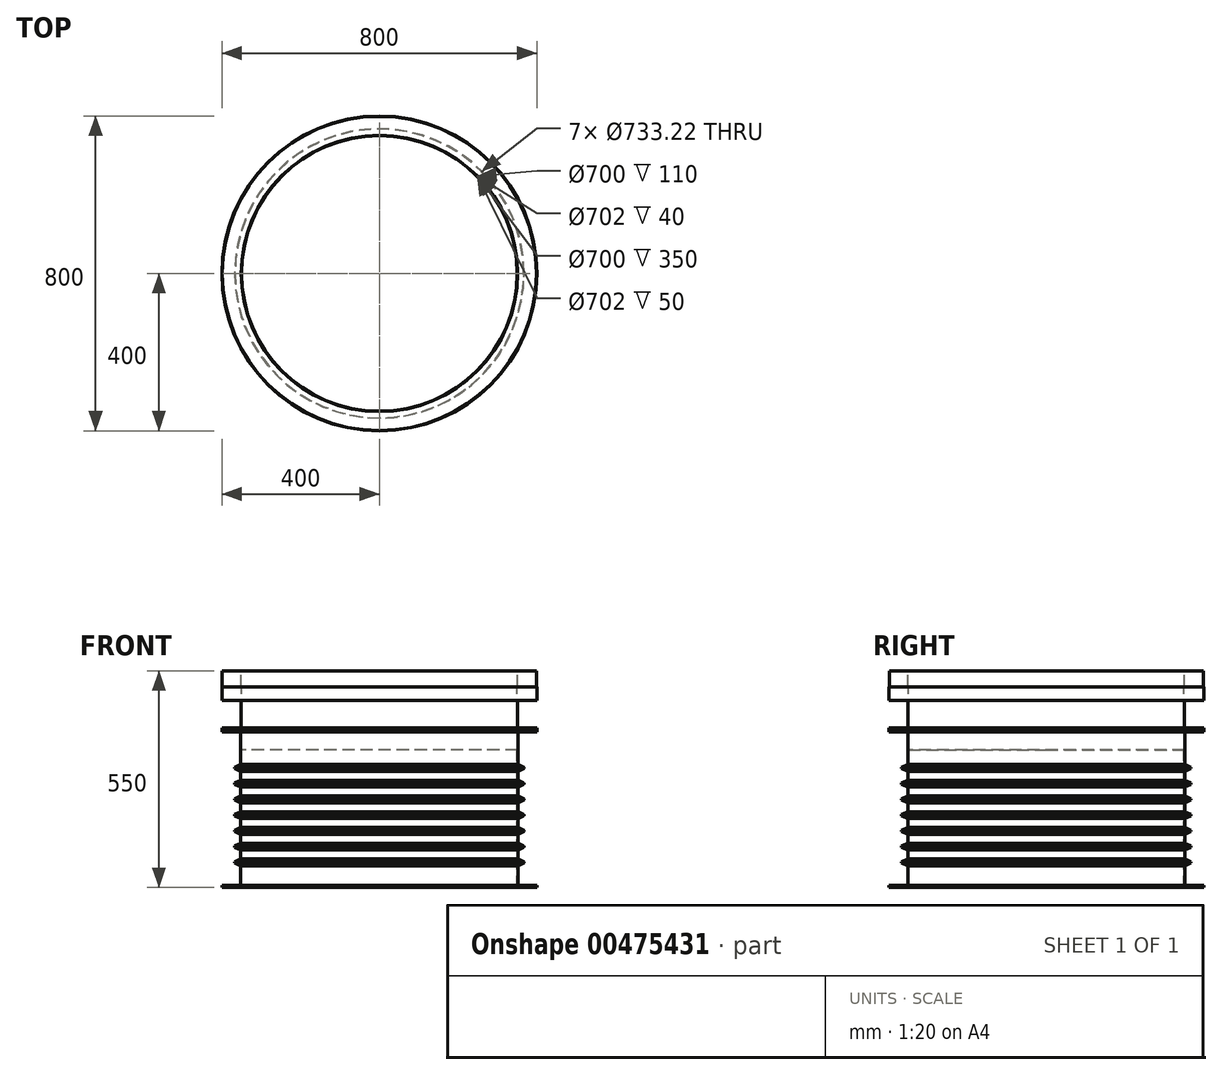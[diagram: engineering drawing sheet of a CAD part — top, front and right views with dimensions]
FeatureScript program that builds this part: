
annotation { "Feature Type Name" : "Feature", "Feature Type Description" : "" }
export const myFeature = defineFeature(function(context is Context, id is Id, definition is map)
    precondition{}
    {
        {
            var Q0;
            Q0=qCreatedBy(makeId("Front.planeOp"),FACE);
            var sketch = newSketch(context, id + "F0", { "sketchPlane" : qUnion([Q0])});
            skLineSegment(sketch, "E0", {"start": v(0, 1099) * mm, "end": v(0, -704.58) * mm, "construction": true});
            skLineSegment(sketch, "E1", {"start": v(-350, 330.96) * mm, "end": v(-350, 680.96) * mm});
            skLineSegment(sketch, "E2", {"start": v(-351, 680.96) * mm, "end": v(-351, 335.96) * mm});
            skLineSegment(sketch, "E3", {"start": v(-351, 335.96) * mm, "end": v(-400, 335.96) * mm});
            skLineSegment(sketch, "E4", {"start": v(-400, 335.96) * mm, "end": v(-400, 330.96) * mm});
            skLineSegment(sketch, "E5", {"start": v(-400, 330.96) * mm, "end": v(-350, 330.96) * mm});
            skLineSegment(sketch, "E6", {"start": v(-350, 680.96) * mm, "end": v(-351, 680.96) * mm});
            skLineSegment(sketch, "E7", {"start": v(-352, 335.96) * mm, "end": v(-352, 385.96) * mm});
            skLineSegment(sketch, "E8", {"start": v(-352, 385.96) * mm, "end": v(-367.6, 393.24) * mm});
            skLineSegment(sketch, "E9", {"start": v(-367.6, 393.24) * mm, "end": v(-367.6, 396.24) * mm});
            skLineSegment(sketch, "E10", {"start": v(-367.6, 396.24) * mm, "end": v(-352, 403.52) * mm});
            skLineSegment(sketch, "E11", {"start": v(-352, 425.96) * mm, "end": v(-352, 403.52) * mm});
            skLineSegment(sketch, "E12", {"start": v(-351, 402.88) * mm, "end": v(-366.6, 395.6) * mm});
            skLineSegment(sketch, "E13", {"start": v(-366.6, 395.6) * mm, "end": v(-366.6, 393.87) * mm});
            skLineSegment(sketch, "E14", {"start": v(-366.6, 393.87) * mm, "end": v(-351, 386.6) * mm});
            skLineSegment(sketch, "E15.0.1.0", {"start": v(-351, 442.88) * mm, "end": v(-366.6, 435.6) * mm});
            skLineSegment(sketch, "E15.0.1.1", {"start": v(-367.6, 436.24) * mm, "end": v(-352, 443.52) * mm});
            skLineSegment(sketch, "E15.0.1.2", {"start": v(-352, 425.96) * mm, "end": v(-367.6, 433.24) * mm});
            skLineSegment(sketch, "E15.0.1.3", {"start": v(-367.6, 433.24) * mm, "end": v(-367.6, 436.24) * mm});
            skLineSegment(sketch, "E15.0.1.4", {"start": v(-352, 465.96) * mm, "end": v(-352, 443.52) * mm});
            skLineSegment(sketch, "E15.0.1.5", {"start": v(-366.6, 433.87) * mm, "end": v(-351, 426.6) * mm});
            skLineSegment(sketch, "E15.0.1.6", {"start": v(-366.6, 435.6) * mm, "end": v(-366.6, 433.87) * mm});
            skLineSegment(sketch, "E15.0.2.0", {"start": v(-351, 482.88) * mm, "end": v(-366.6, 475.6) * mm});
            skLineSegment(sketch, "E15.0.2.1", {"start": v(-367.6, 476.24) * mm, "end": v(-352, 483.52) * mm});
            skLineSegment(sketch, "E15.0.2.2", {"start": v(-352, 465.96) * mm, "end": v(-367.6, 473.24) * mm});
            skLineSegment(sketch, "E15.0.2.3", {"start": v(-367.6, 473.24) * mm, "end": v(-367.6, 476.24) * mm});
            skLineSegment(sketch, "E15.0.2.4", {"start": v(-352, 505.96) * mm, "end": v(-352, 483.52) * mm});
            skLineSegment(sketch, "E15.0.2.5", {"start": v(-366.6, 473.87) * mm, "end": v(-351, 466.6) * mm});
            skLineSegment(sketch, "E15.0.2.6", {"start": v(-366.6, 475.6) * mm, "end": v(-366.6, 473.87) * mm});
            skLineSegment(sketch, "E15.0.3.0", {"start": v(-351, 522.88) * mm, "end": v(-366.6, 515.6) * mm});
            skLineSegment(sketch, "E15.0.3.1", {"start": v(-367.6, 516.24) * mm, "end": v(-352, 523.52) * mm});
            skLineSegment(sketch, "E15.0.3.2", {"start": v(-352, 505.96) * mm, "end": v(-367.6, 513.24) * mm});
            skLineSegment(sketch, "E15.0.3.3", {"start": v(-367.6, 513.24) * mm, "end": v(-367.6, 516.24) * mm});
            skLineSegment(sketch, "E15.0.3.4", {"start": v(-352, 545.96) * mm, "end": v(-352, 523.52) * mm});
            skLineSegment(sketch, "E15.0.3.5", {"start": v(-366.6, 513.87) * mm, "end": v(-351, 506.6) * mm});
            skLineSegment(sketch, "E15.0.3.6", {"start": v(-366.6, 515.6) * mm, "end": v(-366.6, 513.87) * mm});
            skLineSegment(sketch, "E15.0.4.0", {"start": v(-351, 562.88) * mm, "end": v(-366.6, 555.6) * mm});
            skLineSegment(sketch, "E15.0.4.1", {"start": v(-367.6, 556.24) * mm, "end": v(-352, 563.52) * mm});
            skLineSegment(sketch, "E15.0.4.2", {"start": v(-352, 545.96) * mm, "end": v(-367.6, 553.24) * mm});
            skLineSegment(sketch, "E15.0.4.3", {"start": v(-367.6, 553.24) * mm, "end": v(-367.6, 556.24) * mm});
            skLineSegment(sketch, "E15.0.4.4", {"start": v(-352, 585.96) * mm, "end": v(-352, 563.52) * mm});
            skLineSegment(sketch, "E15.0.4.5", {"start": v(-366.6, 553.87) * mm, "end": v(-351, 546.6) * mm});
            skLineSegment(sketch, "E15.0.4.6", {"start": v(-366.6, 555.6) * mm, "end": v(-366.6, 553.87) * mm});
            skLineSegment(sketch, "E15.0.5.0", {"start": v(-351, 602.88) * mm, "end": v(-366.6, 595.6) * mm});
            skLineSegment(sketch, "E15.0.5.1", {"start": v(-367.6, 596.24) * mm, "end": v(-352, 603.52) * mm});
            skLineSegment(sketch, "E15.0.5.2", {"start": v(-352, 585.96) * mm, "end": v(-367.6, 593.24) * mm});
            skLineSegment(sketch, "E15.0.5.3", {"start": v(-367.6, 593.24) * mm, "end": v(-367.6, 596.24) * mm});
            skLineSegment(sketch, "E15.0.5.4", {"start": v(-352, 625.96) * mm, "end": v(-352, 603.52) * mm});
            skLineSegment(sketch, "E15.0.5.5", {"start": v(-366.6, 593.87) * mm, "end": v(-351, 586.6) * mm});
            skLineSegment(sketch, "E15.0.5.6", {"start": v(-366.6, 595.6) * mm, "end": v(-366.6, 593.87) * mm});
            skLineSegment(sketch, "E15.0.6.0", {"start": v(-351, 642.88) * mm, "end": v(-366.6, 635.6) * mm});
            skLineSegment(sketch, "E15.0.6.1", {"start": v(-367.6, 636.24) * mm, "end": v(-352, 643.52) * mm});
            skLineSegment(sketch, "E15.0.6.2", {"start": v(-352, 625.96) * mm, "end": v(-367.6, 633.24) * mm});
            skLineSegment(sketch, "E15.0.6.3", {"start": v(-367.6, 633.24) * mm, "end": v(-367.6, 636.24) * mm});
            skLineSegment(sketch, "E15.0.6.4", {"start": v(-352, 665.96) * mm, "end": v(-352, 643.52) * mm});
            skLineSegment(sketch, "E15.0.6.5", {"start": v(-366.6, 633.87) * mm, "end": v(-351, 626.6) * mm});
            skLineSegment(sketch, "E15.0.6.6", {"start": v(-366.6, 635.6) * mm, "end": v(-366.6, 633.87) * mm});
            skLineSegment(sketch, "E15.direction1", {"start": v(-367.6, 393.24) * mm, "end": v(-342.6, 393.24) * mm, "construction": true});
            skLineSegment(sketch, "E15.direction2", {"start": v(-367.6, 393.24) * mm, "end": v(-367.6, 433.24) * mm, "construction": true});
            skLineSegment(sketch, "E16", {"start": v(-352, 665.96) * mm, "end": v(-352, 725.96) * mm});
            skLineSegment(sketch, "E17", {"start": v(-351, 680.96) * mm, "end": v(-351, 730.96) * mm});
            skLineSegment(sketch, "E18", {"start": v(-350, 730.96) * mm, "end": v(-350, 840.96) * mm});
            skLineSegment(sketch, "E19", {"start": v(-350, 840.96) * mm, "end": v(-351, 840.96) * mm});
            skLineSegment(sketch, "E20", {"start": v(-351, 840.96) * mm, "end": v(-351, 880.96) * mm});
            skLineSegment(sketch, "E21", {"start": v(-351, 880.96) * mm, "end": v(-399, 880.96) * mm});
            skLineSegment(sketch, "E22", {"start": v(-399, 880.96) * mm, "end": v(-399, 840.96) * mm});
            skLineSegment(sketch, "E23", {"start": v(-399, 840.96) * mm, "end": v(-400, 840.96) * mm});
            skLineSegment(sketch, "E24", {"start": v(-400, 840.96) * mm, "end": v(-400, 805.96) * mm});
            skLineSegment(sketch, "E25", {"start": v(-400, 805.96) * mm, "end": v(-351, 805.96) * mm});
            skLineSegment(sketch, "E26", {"start": v(-351, 805.96) * mm, "end": v(-351, 735.96) * mm});
            skLineSegment(sketch, "E27", {"start": v(-352, 730.96) * mm, "end": v(-351, 730.96) * mm});
            skLineSegment(sketch, "E28", {"start": v(-352, 730.96) * mm, "end": v(-400, 730.96) * mm});
            skLineSegment(sketch, "E29", {"start": v(-400, 730.96) * mm, "end": v(-400, 725.96) * mm});
            skLineSegment(sketch, "E30", {"start": v(-400, 725.96) * mm, "end": v(-352, 725.96) * mm});
            skLineSegment(sketch, "E31", {"start": v(-351, 730.96) * mm, "end": v(-350, 730.96) * mm});
            skLineSegment(sketch, "E32", {"start": v(-400, 730.96) * mm, "end": v(-400, 735.96) * mm});
            skLineSegment(sketch, "E33", {"start": v(-400, 735.96) * mm, "end": v(-351, 735.96) * mm});
            skLineSegment(sketch, "E34.trimOffspring", {"start": v(-351, 730.96) * mm, "end": v(-351, 690.96) * mm});
            skSolve(sketch);
        }
        {
            var Q0;
            Q0=makeQuery(id+"F0.imprint","IMPRINT",FACE,{"disambiguationData":[TD([[makeQuery(id+"F0.imprint","IMPRINT",EDGE,{"derivedFrom":sQuery(id+"F0.wireOp",EDGE,"E1")}),1.0]])]});
            var Q1;
            {var subQ6=sQuery(id+"F0.wireOp",EDGE,"E7");Q1=makeQuery(id+"F0.imprint","IMPRINT",FACE,{"disambiguationData":[TD([[makeQuery(id+"F0.imprint","IMPRINT",EDGE,{"derivedFrom":subQ6}),-1.0]])]});}
            var Q2;
            Q2=sQuery(id+"F0.wireOp",EDGE,"E0");
            revolve(context, id + "F1", {"entities" : qUnion([Q0, Q1]), "axis" : qUnion([Q2]), "revolveType" : RevolveType.FULL});
        }
        {
            var Q0;
            Q0=makeQuery(id+"F0.imprint","IMPRINT",FACE,{"disambiguationData":[TD([[makeQuery(id+"F0.imprint","IMPRINT",EDGE,{"derivedFrom":sQuery(id+"F0.wireOp",EDGE,"E18")}),1.0]])]});
            var Q1;
            Q1=sQuery(id+"F0.wireOp",EDGE,"E0");
            revolve(context, id + "F2", {"entities" : qUnion([Q0]), "axis" : qUnion([Q1]), "revolveType" : RevolveType.FULL});
        }
    });
